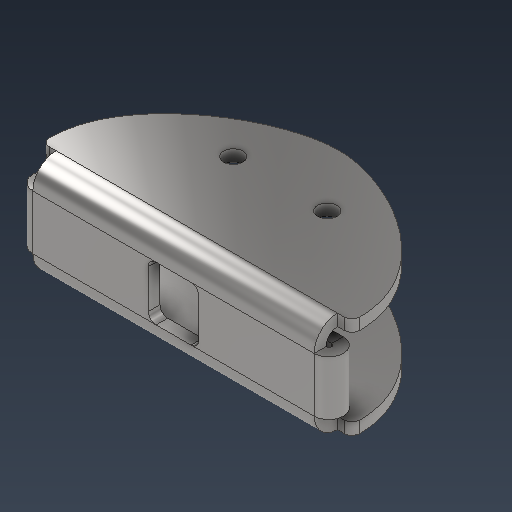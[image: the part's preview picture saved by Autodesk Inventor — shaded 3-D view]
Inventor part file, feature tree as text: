
AUTODESK INVENTOR PART (.ipt)
format: ipt  version: 2021 (Build 250183000, 183)  size: 316,416 bytes
history: native  units: mm
features: sheet_metal_op x9, sketch x9, other x8, fillet x2, hole x1
ambient origin geometry x8: Origin, YZ Plane, XZ Plane, XY Plane, X Axis, Y Axis, Z Axis, Center Point
bodies: Solid1 (feature_tree)
feature tree (29):
  sheet_metal_op  "Face1"
  sheet_metal_op  "Flange1"
  sheet_metal_op  "Flange2"
  sketch  "Sketch4"  dims[d9=6.0mm]
  sheet_metal_op  "Hem1"
  sheet_metal_op  "Hem2"
  hole  "Hole1"  [1 undecoded]
  fillet  "Fillet1"  Radius=42.5mm
  fillet  "Fillet2"  Radius=3.0mm
  other  "midPlane"
  other  "lateralPlane"
  sketch  "Sketch1"  dims[d0=80.0mm d1=40.0mm d2=6.659836mm d5=42.5mm d6=3.0mm]
  other  "Plate1"
  sketch  "Sketch2"  dims[d7=3.0mm]
  other  "Plate2"
  sheet_metal_op  "Bend1"
  sheet_metal_op  "Corner1"
  sketch  "Sketch3"  dims[d8=1.5mm]
  other  "Plate3"
  sheet_metal_op  "Bend2"
  sheet_metal_op  "Corner2"
  sketch  "Sketch7"  dims[d14=12.0mm]
  sketch  "Sketch8"  dims[d15=3.0mm]
  sketch  "Sketch9"  dims[d16=3.0mm d17=3.0mm d18=1.5mm d19=6.0mm d20=3.0mm d21=42.5mm d22=90.0deg d23=3.0mm d24=12.0mm d25=3.0mm d26=3.0mm d27=3.0mm d28=1.5mm d29=6.0mm d30=3.0mm d34=3.0mm d35=1.5mm d36=6.0mm d37=3.0mm d43=3.0mm d44=0.0mm d45=3.0mm d46=0.0mm d47=12.113mm d48=12.113mm d49=27.5mm d50=27.5mm d51=5.0mm d52=6.0mm d53=4.0mm d54=2.0mm d55=90.0deg d56=3.0mm d57=20.594885mm d58=12.0mm d59=1.5mm d60=0.75mm d61=12.0mm d62=1.5mm d63=0.75mm d64=2.0mm d65=3.0mm d66=0.0mm d67=2.0mm d68=14.0mm d69=13.0mm d70=6.5mm d71=26.0mm d72=6.0mm]
  other  "Cut2"
  other  "Cut3"
  other  "Cut4"
  sketch  "Sketch5"  dims[d10=3.0mm]
  sketch  "Sketch6"  dims[d11=26.0mm d12=90.0deg d13=3.0mm]
note: 1 required parameter value undecoded (feature->parameter linkage not recoverable at this tier; creation-order binding heuristic only, values carry confidence <= 0.55)
